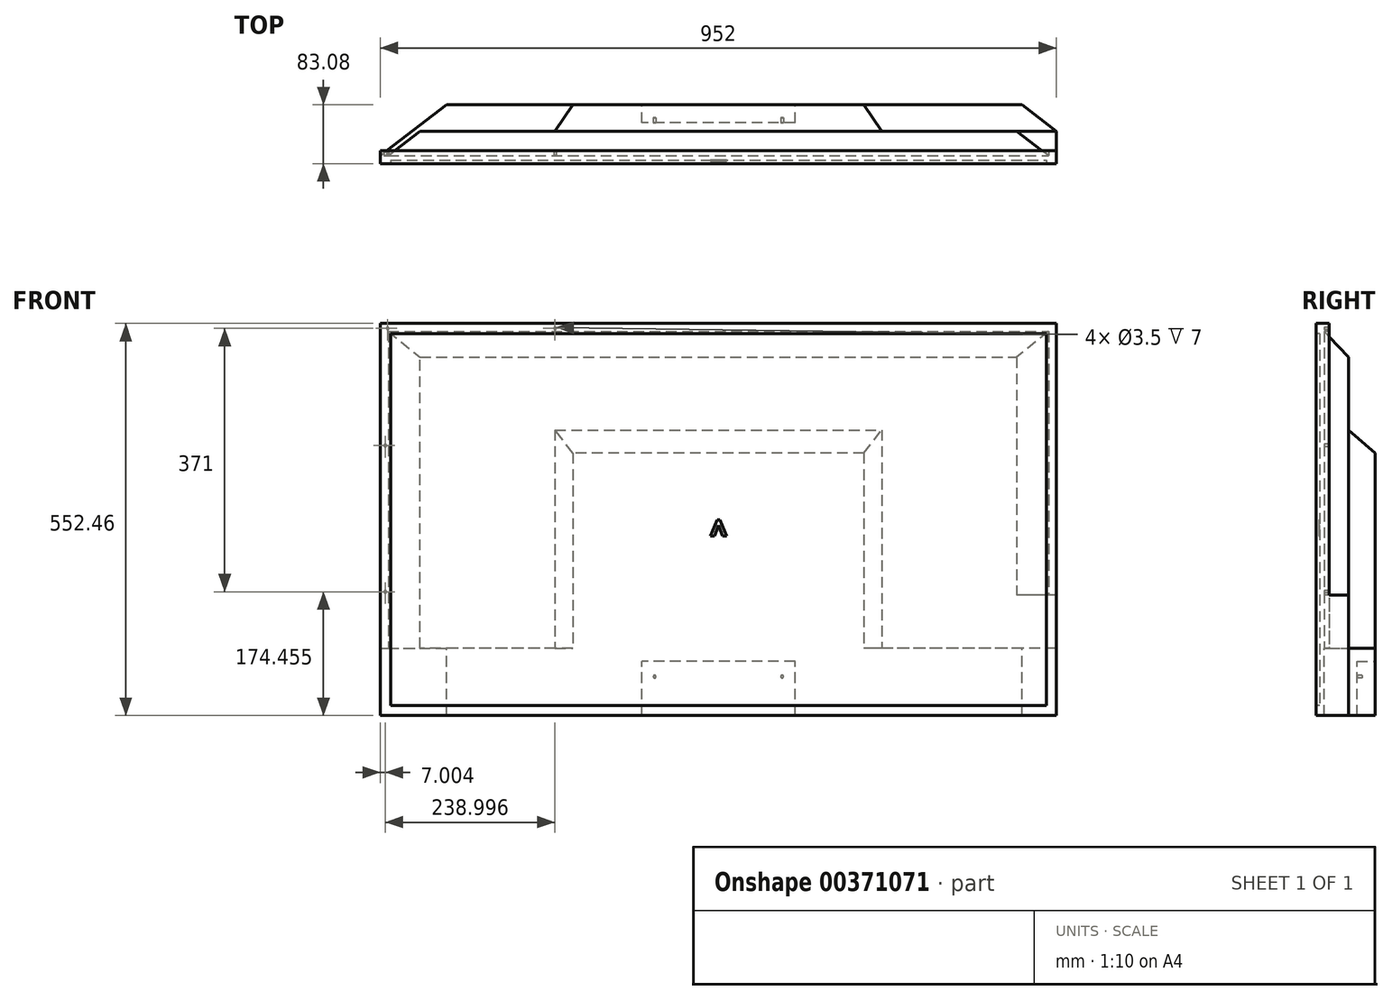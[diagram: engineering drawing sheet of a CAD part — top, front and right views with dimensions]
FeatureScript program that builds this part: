
annotation { "Feature Type Name" : "Feature", "Feature Type Description" : "" }
export const myFeature = defineFeature(function(context is Context, id is Id, definition is map)
    precondition{}
    {
        {
            var Q0;
            Q0=qCreatedBy(makeId("Front.planeOp"),FACE);
            var sketch = newSketch(context, id + "F0", { "sketchPlane" : qUnion([Q0])});
            skLineSegment(sketch, "E0.bottom", {"start": v(476, 276.23) * mm, "end": v(-476, 276.23) * mm});
            skLineSegment(sketch, "E0.top", {"start": v(476, -276.23) * mm, "end": v(-476, -276.23) * mm});
            skLineSegment(sketch, "E0.left", {"start": v(476, 276.23) * mm, "end": v(476, -276.23) * mm});
            skLineSegment(sketch, "E0.right", {"start": v(-476, 276.23) * mm, "end": v(-476, -276.23) * mm});
            skPoint(sketch, "E0.middle", {"position": v(0, 0) * mm});
            skSolve(sketch);
        }
        {
            var Q0;
            Q0=qSketchRegion(id+"F0",true);
            extrude(context, id + "F1", {"entities" : qUnion([Q0]), "oppositeDirection" : true, "depth" : 11.7 * mm});
        }
        {
            var Q0;
            Q0=makeQuery(id+"F1.opExtrude","CAP_FACE",FACE,{"disambiguationData":[OSD([sQuery(id+"F0.wireOp",EDGE,"E0.bottom"),sQuery(id+"F0.wireOp",EDGE,"E0.top"),sQuery(id+"F0.wireOp",EDGE,"E0.left"),sQuery(id+"F0.wireOp",EDGE,"E0.right")])],"isStart":true});
            var sketch = newSketch(context, id + "F2", { "sketchPlane" : qUnion([Q0])});
            skLineSegment(sketch, "E1.bottom", {"start": v(-476, 276.23) * mm, "end": v(476, 276.23) * mm});
            skLineSegment(sketch, "E1.top", {"start": v(-476, -276.23) * mm, "end": v(476, -276.23) * mm});
            skLineSegment(sketch, "E1.left", {"start": v(-476, 276.23) * mm, "end": v(-476, -276.23) * mm});
            skLineSegment(sketch, "E1.right", {"start": v(476, 276.23) * mm, "end": v(476, -276.23) * mm});
            skLineSegment(sketch, "E2.0", {"start": v(-461.7, 261.93) * mm, "end": v(461.7, 261.93) * mm});
            skLineSegment(sketch, "E2.1", {"start": v(-461.7, 261.93) * mm, "end": v(-461.7, -261.93) * mm});
            skLineSegment(sketch, "E2.2", {"start": v(-461.7, -261.93) * mm, "end": v(461.7, -261.93) * mm});
            skLineSegment(sketch, "E2.3", {"start": v(461.7, 261.93) * mm, "end": v(461.7, -261.93) * mm});
            skSolve(sketch);
        }
        {
            var Q0;
            Q0=makeQuery(id+"F2.imprint","IMPRINT",FACE,{"disambiguationData":[TD([[makeQuery(id+"F2.imprint","IMPRINT",EDGE,{"derivedFrom":sQuery(id+"F2.wireOp",EDGE,"E2.0")}),-1.0]])]});
            extrude(context, id + "F3", {"entities" : qUnion([Q0]), "operationType" : NewBodyOperationType.REMOVE, "oppositeDirection" : true, "depth" : 5 * mm});
        }
        {
            var Q0;
            Q0=makeQuery(id+"F3.boolean.opBoolean","COPY",FACE,{"derivedFrom":makeQuery(id+"F3.opExtrude","CAP_FACE",FACE,{"disambiguationData":[OSD([sQuery(id+"F2.wireOp",EDGE,"E2.0"),sQuery(id+"F2.wireOp",EDGE,"E2.1"),sQuery(id+"F2.wireOp",EDGE,"E2.2"),sQuery(id+"F2.wireOp",EDGE,"E2.3")])],"isStart":false})});
            var sketch = newSketch(context, id + "F4", { "sketchPlane" : qUnion([Q0])});
            skText(sketch, "E3", { "text": "^", "fontName": "RobotoSlab-Regular.ttf"});
            const initialGuessF4  = {"E3": [-0.01344, -0.04589, 1, 0, 0.04588]};
            skSetInitialGuess(sketch, initialGuessF4);
            skSolve(sketch);
        }
        {
            var Q0;
            Q0=qSketchRegion(id+"F4",true);
            extrude(context, id + "F5", {"entities" : qUnion([Q0]), "operationType" : NewBodyOperationType.ADD, "depth" : 1 * mm});
        }
        {
            var Q0;
            Q0=makeQuery(id+"F1.opExtrude","CAP_FACE",FACE,{"disambiguationData":[OSD([sQuery(id+"F0.wireOp",EDGE,"E0.bottom"),sQuery(id+"F0.wireOp",EDGE,"E0.top"),sQuery(id+"F0.wireOp",EDGE,"E0.left"),sQuery(id+"F0.wireOp",EDGE,"E0.right")])],"isStart":false});
            var sketch = newSketch(context, id + "F6", { "sketchPlane" : qUnion([Q0])});
            skLineSegment(sketch, "E4.bottom", {"start": v(464.8, 265.03) * mm, "end": v(-464.8, 265.03) * mm});
            skLineSegment(sketch, "E4.top", {"start": v(464.8, -265.03) * mm, "end": v(-464.8, -265.03) * mm});
            skLineSegment(sketch, "E4.left", {"start": v(464.8, 265.03) * mm, "end": v(464.8, -265.03) * mm});
            skLineSegment(sketch, "E4.right", {"start": v(-464.8, 265.03) * mm, "end": v(-464.8, -265.03) * mm});
            skPoint(sketch, "E4.middle", {"position": v(0, 0) * mm});
            skLineSegment(sketch, "E5.top", {"start": v(-476, -106.23) * mm, "end": v(0, -106.23) * mm});
            skLineSegment(sketch, "E5.left", {"start": v(-476, -276.23) * mm, "end": v(-476, -106.23) * mm});
            skLineSegment(sketch, "E5.right", {"start": v(0, -276.23) * mm, "end": v(0, -106.23) * mm});
            skLineSegment(sketch, "E6.top", {"start": v(476, -181.22) * mm, "end": v(0, -181.22) * mm});
            skLineSegment(sketch, "E6.left", {"start": v(476, -276.23) * mm, "end": v(476, -181.22) * mm});
            skSolve(sketch);
        }
        {
            var Q0;
            Q0=qSketchRegion(id+"F6",true);
            var Q1;
            {var subQ0=sQuery(id+"F6.wireOp",EDGE,"E5.left");Q1=makeQuery(id+"F6.imprint","IMPRINT",FACE,{"disambiguationData":[TD([[makeQuery(id+"F6.imprint","IMPRINT",EDGE,{"derivedFrom":subQ0}),1.0]])]});}
            var Q2;
            {var subQ0=sQuery(id+"F6.wireOp",EDGE,"E6.left");Q2=makeQuery(id+"F6.imprint","IMPRINT",FACE,{"disambiguationData":[TD([[makeQuery(id+"F6.imprint","IMPRINT",EDGE,{"derivedFrom":subQ0}),-1.0]])]});}
            extrude(context, id + "F7", {"entities" : qUnion([Q0, Q1, Q2]), "operationType" : NewBodyOperationType.ADD, "depth" : 34.34 * mm});
        }
        {
            var Q0;
            Q0=makeQuery(id+"F7.opExtrude","SWEPT_FACE",FACE,{"disambiguationData":[OSD([sQuery(id+"F6.wireOp",EDGE,"E4.bottom")])]});
            var sketch = newSketch(context, id + "F8", { "sketchPlane" : qUnion([Q0])});
            skLineSegment(sketch, "E7", {"start": v(-464.8, 11.7) * mm, "end": v(-420.03, 46.04) * mm});
            skLineSegment(sketch, "E8", {"start": v(-420.03, 46.04) * mm, "end": v(-464.8, 46.04) * mm});
            skLineSegment(sketch, "E9", {"start": v(-464.8, 46.04) * mm, "end": v(-464.8, 11.7) * mm});
            skSolve(sketch);
        }
        {
            var Q0;
            Q0=makeQuery(id+"F8.imprint","IMPRINT",FACE,{"disambiguationData":[TD([[makeQuery(id+"F8.imprint","IMPRINT",EDGE,{"derivedFrom":sQuery(id+"F8.wireOp",EDGE,"E7")}),1.0]])]});
            var Q1;
            Q1=makeQuery(id+"F7.opExtrude","SWEPT_FACE",FACE,{"disambiguationData":[OSD([sQuery(id+"F6.wireOp",EDGE,"E6.top")])]});
            extrude(context, id + "F9", {"entities" : qUnion([Q0]), "operationType" : NewBodyOperationType.REMOVE, "endBound" : BoundingType.UP_TO_SURFACE, "oppositeDirection" : true, "endBoundEntityFace" : qUnion([Q1]), "depth" : 400 * mm});
        }
        {
            var Q0;
            Q0=makeQuery(id+"F7.opExtrude","SWEPT_FACE",FACE,{"disambiguationData":[OSD([sQuery(id+"F6.wireOp",EDGE,"E4.right")])]});
            var sketch = newSketch(context, id + "F10", { "sketchPlane" : qUnion([Q0])});
            skLineSegment(sketch, "E10", {"start": v(11.7, 265.03) * mm, "end": v(46.04, 228.6) * mm});
            skLineSegment(sketch, "E11", {"start": v(46.04, 228.6) * mm, "end": v(46.04, 265.03) * mm});
            skLineSegment(sketch, "E12", {"start": v(46.04, 265.03) * mm, "end": v(11.7, 265.03) * mm});
            skSolve(sketch);
        }
        {
            var Q0;
            Q0=makeQuery(id+"F10.imprint","IMPRINT",FACE,{"disambiguationData":[TD([[makeQuery(id+"F10.imprint","IMPRINT",EDGE,{"derivedFrom":sQuery(id+"F10.wireOp",EDGE,"E10")}),1.0]])]});
            var Q1;
            Q1=makeQuery(id+"F7.boolean.opBoolean","MERGE",FACE,{"derivedFrom":[makeQuery(id+"F1.opExtrude","SWEPT_FACE",FACE,{"disambiguationData":[OSD([sQuery(id+"F0.wireOp",EDGE,"E0.right")])]}),makeQuery(id+"F7.opExtrude","SWEPT_FACE",FACE,{"disambiguationData":[OSD([sQuery(id+"F6.wireOp",EDGE,"E6.left")])]})]});
            extrude(context, id + "F11", {"entities" : qUnion([Q0]), "operationType" : NewBodyOperationType.REMOVE, "endBound" : BoundingType.UP_TO_SURFACE, "oppositeDirection" : true, "endBoundEntityFace" : qUnion([Q1]), "depth" : 25 * mm});
        }
        {
            var Q0;
            Q0=makeQuery(id+"F7.opExtrude","SWEPT_FACE",FACE,{"disambiguationData":[OSD([sQuery(id+"F6.wireOp",EDGE,"E5.top")])]});
            var sketch = newSketch(context, id + "F12", { "sketchPlane" : qUnion([Q0])});
            skLineSegment(sketch, "E13", {"start": v(464.8, 11.7) * mm, "end": v(420.03, 46.04) * mm});
            skLineSegment(sketch, "E14", {"start": v(420.03, 46.04) * mm, "end": v(464.8, 46.04) * mm});
            skLineSegment(sketch, "E15", {"start": v(464.8, 46.04) * mm, "end": v(464.8, 11.7) * mm});
            skSolve(sketch);
        }
        {
            var Q0;
            Q0=qSketchRegion(id+"F12",true);
            var Q1;
            Q1=makeQuery(id+"F1.opExtrude","SWEPT_FACE",FACE,{"disambiguationData":[OSD([sQuery(id+"F0.wireOp",EDGE,"E0.bottom")])]});
            extrude(context, id + "F13", {"entities" : qUnion([Q0]), "operationType" : NewBodyOperationType.REMOVE, "endBound" : BoundingType.UP_TO_SURFACE, "endBoundEntityFace" : qUnion([Q1]), "depth" : 25 * mm});
        }
        {
            var Q0;
            Q0=makeQuery(id+"F7.opExtrude","CAP_FACE",FACE,{"disambiguationData":[OSD([sQuery(id+"F0.wireOp",EDGE,"E0.top"),sQuery(id+"F6.wireOp",EDGE,"E4.bottom"),sQuery(id+"F6.wireOp",EDGE,"E4.left"),sQuery(id+"F6.wireOp",EDGE,"E4.right"),sQuery(id+"F6.wireOp",EDGE,"E5.top"),sQuery(id+"F6.wireOp",EDGE,"E5.left"),sQuery(id+"F6.wireOp",EDGE,"E6.top"),sQuery(id+"F6.wireOp",EDGE,"E6.left")])],"isStart":false});
            var sketch = newSketch(context, id + "F14", { "sketchPlane" : qUnion([Q0])});
            skLineSegment(sketch, "E16.bottom", {"start": v(230, 126.23) * mm, "end": v(-230, 126.23) * mm});
            skLineSegment(sketch, "E16.top", {"start": v(230, -126.23) * mm, "end": v(-230, -126.23) * mm});
            skLineSegment(sketch, "E16.left", {"start": v(230, 126.23) * mm, "end": v(230, -126.23) * mm});
            skLineSegment(sketch, "E16.right", {"start": v(-230, 126.23) * mm, "end": v(-230, -126.23) * mm});
            skPoint(sketch, "E16.middle", {"position": v(0, 0) * mm});
            skLineSegment(sketch, "E17.bottom", {"start": v(-476, -276.23) * mm, "end": v(476, -276.23) * mm});
            skLineSegment(sketch, "E17.top", {"start": v(-476, -181.22) * mm, "end": v(476, -181.22) * mm});
            skLineSegment(sketch, "E17.left", {"start": v(-476, -276.23) * mm, "end": v(-476, -181.22) * mm});
            skLineSegment(sketch, "E17.right", {"start": v(476, -276.23) * mm, "end": v(476, -181.22) * mm});
            skLineSegment(sketch, "E18", {"start": v(-230, -126.23) * mm, "end": v(-230, -181.22) * mm});
            skLineSegment(sketch, "E19", {"start": v(230, -126.23) * mm, "end": v(230, -181.22) * mm});
            skSolve(sketch);
        }
        {
            var Q0;
            Q0=qSketchRegion(id+"F14",true);
            extrude(context, id + "F15", {"entities" : qUnion([Q0]), "operationType" : NewBodyOperationType.ADD, "depth" : 37.05 * mm});
        }
        {
            var Q0;
            {var subQ0=sQuery(id+"F14.wireOp",EDGE,"E17.top");var subQ2=sQuery(id+"F6.wireOp",EDGE,"E6.top");Q0=makeQuery(id+"F15.boolean.opBoolean","MERGE",FACE,{"derivedFrom":[makeQuery(id+"F9.boolean.opBoolean","MERGE",FACE,{"derivedFrom":[makeQuery(id+"F7.opExtrude","SWEPT_FACE",FACE,{"disambiguationData":[OSD([subQ2])]}),makeQuery(id+"F9.opExtrude","CAP_FACE",FACE,{"disambiguationData":[OSD([subQ2])],"isStart":false})]}),makeQuery(id+"F15.opExtrude","SWEPT_FACE",FACE,{"disambiguationData":[OSD([subQ0]),TDD([makeQuery(id+"F14.imprint","IMPRINT",EDGE,{"disambiguationData":[TD([[makeQuery(id+"F14.imprint","INTERSECT",VERTEX,{"derivedFrom":[subQ0,sQuery(id+"F14.wireOp",EDGE,"E17.right")]}),-1.0]])],"derivedFrom":subQ0}),makeQuery(id+"F14.imprint","IMPRINT",EDGE,{"disambiguationData":[TD([[makeQuery(id+"F14.imprint","INTERSECT",VERTEX,{"derivedFrom":[subQ0,sQuery(id+"F14.wireOp",EDGE,"E19")]}),-1.0]])],"derivedFrom":subQ0})])]})]});}
            var sketch = newSketch(context, id + "F16", { "sketchPlane" : qUnion([Q0])});
            skLineSegment(sketch, "E20", {"start": v(-476, 11.7) * mm, "end": v(-384.43, 81.94) * mm});
            skLineSegment(sketch, "E21", {"start": v(-384.43, 81.94) * mm, "end": v(-382.93, 83.08) * mm});
            skLineSegment(sketch, "E22", {"start": v(-382.93, 83.08) * mm, "end": v(-476, 83.08) * mm});
            skLineSegment(sketch, "E23", {"start": v(-476, 83.08) * mm, "end": v(-476, 11.7) * mm});
            skSolve(sketch);
        }
        {
            var Q0;
            Q0=makeQuery(id+"F16.imprint","IMPRINT",FACE,{"disambiguationData":[TD([[makeQuery(id+"F16.imprint","IMPRINT",EDGE,{"derivedFrom":sQuery(id+"F16.wireOp",EDGE,"E20")}),1.0]])]});
            var Q1;
            {var subQ0=sQuery(id+"F0.wireOp",EDGE,"E0.top");Q1=makeQuery(id+"F15.boolean.opBoolean","MERGE",FACE,{"derivedFrom":[makeQuery(id+"F7.boolean.opBoolean","MERGE",FACE,{"derivedFrom":[makeQuery(id+"F1.opExtrude","SWEPT_FACE",FACE,{"disambiguationData":[OSD([subQ0])]}),makeQuery(id+"F7.opExtrude","SWEPT_FACE",FACE,{"disambiguationData":[OSD([subQ0])]})]}),makeQuery(id+"F15.opExtrude","SWEPT_FACE",FACE,{"disambiguationData":[OSD([sQuery(id+"F14.wireOp",EDGE,"E17.bottom")])]})]});}
            extrude(context, id + "F17", {"entities" : qUnion([Q0]), "operationType" : NewBodyOperationType.REMOVE, "endBound" : BoundingType.UP_TO_SURFACE, "oppositeDirection" : true, "endBoundEntityFace" : qUnion([Q1]), "depth" : 25 * mm});
        }
        {
            var Q0;
            Q0=makeQuery(id+"F15.opExtrude","SWEPT_FACE",FACE,{"disambiguationData":[OSD([sQuery(id+"F14.wireOp",EDGE,"E16.left"),sQuery(id+"F14.wireOp",EDGE,"E19")])]});
            var sketch = newSketch(context, id + "F18", { "sketchPlane" : qUnion([Q0])});
            skLineSegment(sketch, "E24", {"start": v(-46.04, 126.23) * mm, "end": v(-83.08, 93.77) * mm});
            skLineSegment(sketch, "E25", {"start": v(-83.08, 93.77) * mm, "end": v(-83.08, 126.23) * mm});
            skLineSegment(sketch, "E26", {"start": v(-83.08, 126.23) * mm, "end": v(-46.04, 126.23) * mm});
            skSolve(sketch);
        }
        {
            var Q0;
            Q0=makeQuery(id+"F18.imprint","IMPRINT",FACE,{"disambiguationData":[TD([[makeQuery(id+"F18.imprint","IMPRINT",EDGE,{"derivedFrom":sQuery(id+"F18.wireOp",EDGE,"E24")}),-1.0]])]});
            var Q1;
            Q1=makeQuery(id+"F15.opExtrude","SWEPT_FACE",FACE,{"disambiguationData":[OSD([sQuery(id+"F14.wireOp",EDGE,"E16.right"),sQuery(id+"F14.wireOp",EDGE,"E18")])]});
            extrude(context, id + "F19", {"entities" : qUnion([Q0]), "operationType" : NewBodyOperationType.REMOVE, "endBound" : BoundingType.UP_TO_SURFACE, "oppositeDirection" : true, "endBoundEntityFace" : qUnion([Q1]), "depth" : 25 * mm});
        }
        {
            var Q0;
            {var subQ0=sQuery(id+"F14.wireOp",EDGE,"E17.top");var subQ2=sQuery(id+"F6.wireOp",EDGE,"E6.top");Q0=makeQuery(id+"F15.boolean.opBoolean","MERGE",FACE,{"derivedFrom":[makeQuery(id+"F9.boolean.opBoolean","MERGE",FACE,{"derivedFrom":[makeQuery(id+"F7.opExtrude","SWEPT_FACE",FACE,{"disambiguationData":[OSD([subQ2])]}),makeQuery(id+"F9.opExtrude","CAP_FACE",FACE,{"disambiguationData":[OSD([subQ2])],"isStart":false})]}),makeQuery(id+"F15.opExtrude","SWEPT_FACE",FACE,{"disambiguationData":[OSD([subQ0]),TDD([makeQuery(id+"F14.imprint","IMPRINT",EDGE,{"disambiguationData":[TD([[makeQuery(id+"F14.imprint","INTERSECT",VERTEX,{"derivedFrom":[subQ0,sQuery(id+"F14.wireOp",EDGE,"E17.right")]}),-1.0]])],"derivedFrom":subQ0}),makeQuery(id+"F14.imprint","IMPRINT",EDGE,{"disambiguationData":[TD([[makeQuery(id+"F14.imprint","INTERSECT",VERTEX,{"derivedFrom":[subQ0,sQuery(id+"F14.wireOp",EDGE,"E19")]}),-1.0]])],"derivedFrom":subQ0})])]})]});}
            var sketch = newSketch(context, id + "F20", { "sketchPlane" : qUnion([Q0])});
            skLineSegment(sketch, "E27", {"start": v(-230, 46.04) * mm, "end": v(-205, 83.08) * mm});
            skLineSegment(sketch, "E28", {"start": v(-205, 83.08) * mm, "end": v(-230, 83.08) * mm});
            skLineSegment(sketch, "E29", {"start": v(-230, 83.08) * mm, "end": v(-230, 46.04) * mm});
            skLineSegment(sketch, "E30.MirrorCS", {"start": v(205, 83.08) * mm, "end": v(230, 83.08) * mm});
            skLineSegment(sketch, "E31.MirrorCS", {"start": v(230, 83.08) * mm, "end": v(230, 46.04) * mm});
            skLineSegment(sketch, "E32.MirrorCS", {"start": v(230, 46.04) * mm, "end": v(205, 83.08) * mm});
            skSolve(sketch);
        }
        {
            var Q0;
            Q0=qSketchRegion(id+"F20",true);
            var Q1;
            Q1=makeQuery(id+"F1.opExtrude","SWEPT_FACE",FACE,{"disambiguationData":[OSD([sQuery(id+"F0.wireOp",EDGE,"E0.bottom")])]});
            extrude(context, id + "F21", {"entities" : qUnion([Q0]), "operationType" : NewBodyOperationType.REMOVE, "endBound" : BoundingType.UP_TO_SURFACE, "endBoundEntityFace" : qUnion([Q1]), "depth" : 25 * mm});
        }
        {
            var Q0;
            {var subQ0=sQuery(id+"F14.wireOp",EDGE,"E17.top");Q0=makeQuery(id+"F21.boolean.opBoolean","MERGE",FACE,{"derivedFrom":[makeQuery(id+"F15.opExtrude","SWEPT_FACE",FACE,{"disambiguationData":[OSD([subQ0]),TDD([makeQuery(id+"F14.imprint","IMPRINT",EDGE,{"disambiguationData":[TD([[makeQuery(id+"F14.imprint","INTERSECT",VERTEX,{"derivedFrom":[subQ0,sQuery(id+"F14.wireOp",EDGE,"E18")]}),1.0]])],"derivedFrom":subQ0})])]}),makeQuery(id+"F21.opExtrude","CAP_FACE",FACE,{"disambiguationData":[OSD([sQuery(id+"F20.wireOp",EDGE,"E30.MirrorCS"),sQuery(id+"F20.wireOp",EDGE,"E31.MirrorCS"),sQuery(id+"F20.wireOp",EDGE,"E32.MirrorCS")])],"isStart":true})]});}
            var sketch = newSketch(context, id + "F22", { "sketchPlane" : qUnion([Q0])});
            skLineSegment(sketch, "E33", {"start": v(476, 46.04) * mm, "end": v(427.7, 83.08) * mm});
            skLineSegment(sketch, "E34", {"start": v(427.7, 83.08) * mm, "end": v(476, 83.08) * mm});
            skLineSegment(sketch, "E35", {"start": v(476, 83.08) * mm, "end": v(476, 46.04) * mm});
            skSolve(sketch);
        }
        {
            var Q0;
            Q0=qSketchRegion(id+"F22",true);
            var Q1;
            {var subQ0=sQuery(id+"F0.wireOp",EDGE,"E0.top");Q1=makeQuery(id+"F15.boolean.opBoolean","MERGE",FACE,{"derivedFrom":[makeQuery(id+"F7.boolean.opBoolean","MERGE",FACE,{"derivedFrom":[makeQuery(id+"F1.opExtrude","SWEPT_FACE",FACE,{"disambiguationData":[OSD([subQ0])]}),makeQuery(id+"F7.opExtrude","SWEPT_FACE",FACE,{"disambiguationData":[OSD([subQ0])]})]}),makeQuery(id+"F15.opExtrude","SWEPT_FACE",FACE,{"disambiguationData":[OSD([sQuery(id+"F14.wireOp",EDGE,"E17.bottom")])]})]});}
            extrude(context, id + "F23", {"entities" : qUnion([Q0]), "operationType" : NewBodyOperationType.REMOVE, "endBound" : BoundingType.UP_TO_SURFACE, "oppositeDirection" : true, "endBoundEntityFace" : qUnion([Q1]), "depth" : 25 * mm});
        }
        {
            var Q0;
            Q0=makeQuery(id+"F1.opExtrude","CAP_FACE",FACE,{"disambiguationData":[OSD([sQuery(id+"F0.wireOp",EDGE,"E0.bottom"),sQuery(id+"F0.wireOp",EDGE,"E0.top"),sQuery(id+"F0.wireOp",EDGE,"E0.left"),sQuery(id+"F0.wireOp",EDGE,"E0.right")])],"isStart":false});
            var sketch = newSketch(context, id + "F24", { "sketchPlane" : qUnion([Q0])});
            skCircle(sketch, "E36", {"center": v(-465.65, 269.23) * mm, "radius": 1.75 * mm});
            skCircle(sketch, "E37", {"center": v(-469, 104.23) * mm, "radius": 1.75 * mm});
            skCircle(sketch, "E38", {"center": v(-469, -101.77) * mm, "radius": 1.75 * mm});
            skCircle(sketch, "E39", {"center": v(-230, 269.23) * mm, "radius": 1.75 * mm});
            skCircle(sketch, "E40", {"center": v(0, 269.23) * mm, "radius": 1.75 * mm});
            skCircle(sketch, "E41.MirrorC", {"center": v(469, -101.77) * mm, "radius": 1.75 * mm});
            skCircle(sketch, "E42.MirrorC", {"center": v(469, 104.23) * mm, "radius": 1.75 * mm});
            skCircle(sketch, "E43.MirrorC", {"center": v(465.65, 269.23) * mm, "radius": 1.75 * mm});
            skCircle(sketch, "E44.MirrorC", {"center": v(230, 269.23) * mm, "radius": 1.75 * mm});
            skSolve(sketch);
        }
        {
            var Q0;
            Q0=makeQuery(id+"F24.imprint","IMPRINT",FACE,{"disambiguationData":[TD([[makeQuery(id+"F24.imprint","IMPRINT",EDGE,{"derivedFrom":sQuery(id+"F24.wireOp",EDGE,"E36")}),1.0]])]});
            var Q1;
            Q1=makeQuery(id+"F24.imprint","IMPRINT",FACE,{"disambiguationData":[TD([[makeQuery(id+"F24.imprint","IMPRINT",EDGE,{"derivedFrom":sQuery(id+"F24.wireOp",EDGE,"E37")}),1.0]])]});
            var Q2;
            Q2=makeQuery(id+"F24.imprint","IMPRINT",FACE,{"disambiguationData":[TD([[makeQuery(id+"F24.imprint","IMPRINT",EDGE,{"derivedFrom":sQuery(id+"F24.wireOp",EDGE,"E38")}),1.0]])]});
            var Q3;
            Q3=makeQuery(id+"F24.imprint","IMPRINT",FACE,{"disambiguationData":[TD([[makeQuery(id+"F24.imprint","IMPRINT",EDGE,{"derivedFrom":sQuery(id+"F24.wireOp",EDGE,"E39")}),1.0]])]});
            var Q4;
            Q4=makeQuery(id+"F24.imprint","IMPRINT",FACE,{"disambiguationData":[TD([[makeQuery(id+"F24.imprint","IMPRINT",EDGE,{"derivedFrom":sQuery(id+"F24.wireOp",EDGE,"E40")}),1.0]])]});
            var Q5;
            Q5=makeQuery(id+"F24.imprint","IMPRINT",FACE,{"disambiguationData":[TD([[makeQuery(id+"F24.imprint","IMPRINT",EDGE,{"derivedFrom":sQuery(id+"F24.wireOp",EDGE,"E44.MirrorC")}),-1.0]])]});
            var Q6;
            Q6=makeQuery(id+"F24.imprint","IMPRINT",FACE,{"disambiguationData":[TD([[makeQuery(id+"F24.imprint","IMPRINT",EDGE,{"derivedFrom":sQuery(id+"F24.wireOp",EDGE,"E43.MirrorC")}),-1.0]])]});
            var Q7;
            Q7=makeQuery(id+"F24.imprint","IMPRINT",FACE,{"disambiguationData":[TD([[makeQuery(id+"F24.imprint","IMPRINT",EDGE,{"derivedFrom":sQuery(id+"F24.wireOp",EDGE,"E42.MirrorC")}),-1.0]])]});
            var Q8;
            Q8=makeQuery(id+"F24.imprint","IMPRINT",FACE,{"disambiguationData":[TD([[makeQuery(id+"F24.imprint","IMPRINT",EDGE,{"derivedFrom":sQuery(id+"F24.wireOp",EDGE,"E41.MirrorC")}),-1.0]])]});
            extrude(context, id + "F25", {"entities" : qUnion([Q0, Q1, Q2, Q3, Q4, Q5, Q6, Q7, Q8]), "operationType" : NewBodyOperationType.ADD, "depth" : 7 * mm});
        }
        {
            var Q0;
            Q0=makeQuery(id+"F15.opExtrude","CAP_FACE",FACE,{"disambiguationData":[OSD([sQuery(id+"F14.wireOp",EDGE,"E16.bottom"),sQuery(id+"F14.wireOp",EDGE,"E16.left"),sQuery(id+"F14.wireOp",EDGE,"E16.right"),sQuery(id+"F14.wireOp",EDGE,"E17.bottom"),sQuery(id+"F14.wireOp",EDGE,"E17.top"),sQuery(id+"F14.wireOp",EDGE,"E17.left"),sQuery(id+"F14.wireOp",EDGE,"E17.right"),sQuery(id+"F14.wireOp",EDGE,"E18"),sQuery(id+"F14.wireOp",EDGE,"E19")])],"isStart":false});
            var sketch = newSketch(context, id + "F26", { "sketchPlane" : qUnion([Q0])});
            skLineSegment(sketch, "E45.bottom", {"start": v(-107.95, -276.23) * mm, "end": v(107.95, -276.23) * mm});
            skLineSegment(sketch, "E45.top", {"start": v(-107.95, -200.03) * mm, "end": v(107.95, -200.03) * mm});
            skLineSegment(sketch, "E45.left", {"start": v(-107.95, -276.23) * mm, "end": v(-107.95, -200.03) * mm});
            skLineSegment(sketch, "E45.right", {"start": v(107.95, -276.23) * mm, "end": v(107.95, -200.03) * mm});
            skSolve(sketch);
        }
        {
            var Q0;
            Q0=qSketchRegion(id+"F26",true);
            extrude(context, id + "F27", {"entities" : qUnion([Q0]), "operationType" : NewBodyOperationType.REMOVE, "oppositeDirection" : true, "depth" : 25.4 * mm});
        }
        {
            var Q0;
            Q0=makeQuery(id+"F27.boolean.opBoolean","COPY",FACE,{"derivedFrom":makeQuery(id+"F27.opExtrude","CAP_FACE",FACE,{"disambiguationData":[OSD([sQuery(id+"F26.wireOp",EDGE,"E45.bottom"),sQuery(id+"F26.wireOp",EDGE,"E45.top"),sQuery(id+"F26.wireOp",EDGE,"E45.left"),sQuery(id+"F26.wireOp",EDGE,"E45.right")])],"isStart":false})});
            var sketch = newSketch(context, id + "F28", { "sketchPlane" : qUnion([Q0])});
            skCircle(sketch, "E46", {"center": v(-89.7, -221.23) * mm, "radius": 1.92 * mm});
            skCircle(sketch, "E47.MirrorC", {"center": v(89.7, -221.23) * mm, "radius": 1.92 * mm});
            skSolve(sketch);
        }
        {
            var Q0;
            Q0=qSketchRegion(id+"F28",true);
            extrude(context, id + "F29", {"entities" : qUnion([Q0]), "operationType" : NewBodyOperationType.ADD, "depth" : 7 * mm});
        }
    });
